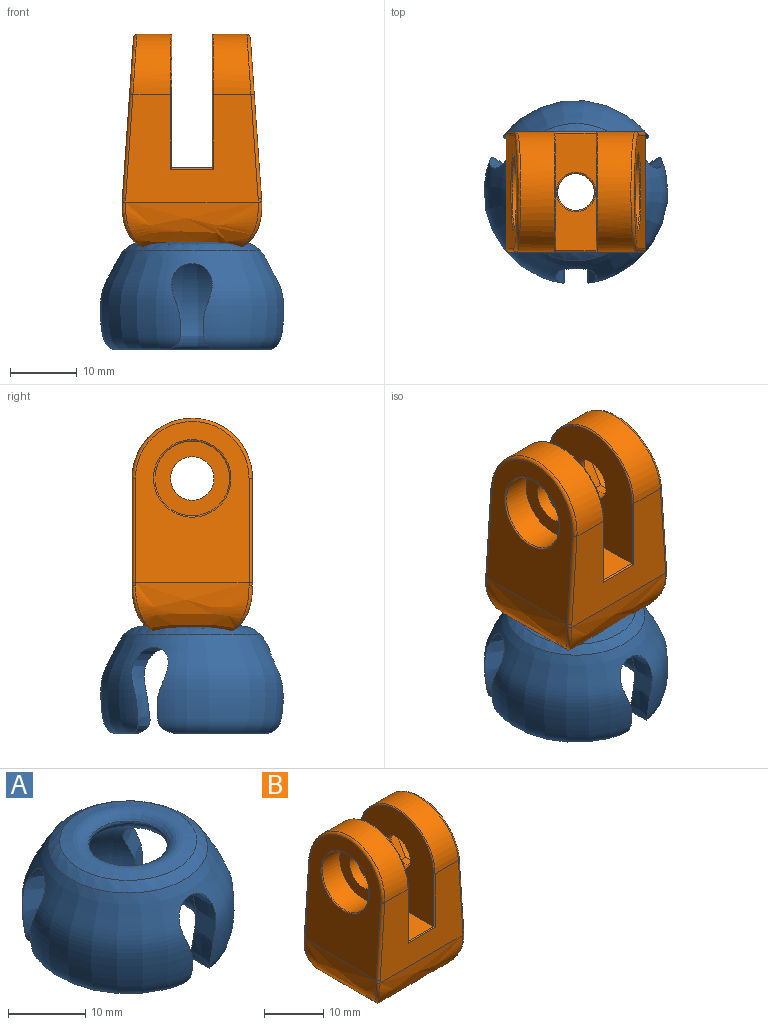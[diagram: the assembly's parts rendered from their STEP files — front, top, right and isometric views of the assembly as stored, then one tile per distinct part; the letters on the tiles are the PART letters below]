
ASSEMBLY  parts=2 mates=1
PART A: 9 faces, bbox 27.5x27.5x16.2 mm
  f0: revolved ~27.48x27.48mm, area 1956.7mm2, adj f1,f2,f3,f4,f5,f6,f7,f8
  f1: revolved ~20.56x20.56mm, area 105.4mm2, adj f0,f2
  f2: revolved ~17.76x17.76mm, area 177mm2, adj f0,f1
  f3: extruded ~12.89x6.51mm, area 55.8mm2, adj f0,f4
  f4: extruded ~12.89x6.51mm, area 55.8mm2, adj f0,f3
  f5: extruded ~12.89x7.44mm, area 55.8mm2, adj f0,f6
  f6: extruded ~12.89x7.44mm, area 55.8mm2, adj f0,f5
  f7: extruded ~12.89x7.44mm, area 55.8mm2, adj f0,f8
  f8: extruded ~12.89x7.44mm, area 55.8mm2, adj f0,f7
PART B: 57 faces, bbox 22x19.5x33.7 mm
  f0: plane 4.89x3mm, normal (0,-0.87,0.5), area 17mm2, adj f1,f5,f19,f21
  f1: plane 4.89x3mm, normal (0,-0.87,-0.5), area 17mm2, adj f0,f2,f19,f22
  f2: plane 5.65x3mm, normal (0,0,-1), area 16.9mm2, adj f1,f3,f19,f23
  f3: plane 4.89x3mm, normal (0,0.87,-0.5), area 17mm2, adj f2,f4,f19,f24
  f4: plane 4.89x3mm, normal (0,0.87,0.5), area 17mm2, adj f3,f5,f19,f25
  f5: plane 5.65x3mm, normal (0,0,1), area 16.9mm2, adj f0,f4,f19,f26
  f6: cylinder r=3.25mm len=6.5mm, axis (1,0,0), area 40.3mm2, adj f12,f19
  f7: cylinder r=9mm len=18mm, axis (-1,0,0), area 158.4mm2, adj f8,f11,f28,f38
  f8: plane 19.89x16.1mm, normal (0,-1,0), area 230.2mm2, adj f7,f10,f29,f32,f33,f34,f36,f45
  f9: cylinder r=3.25mm len=6.5mm, axis (1,0,0), area 40.3mm2, adj f13,f17
  f10: cylinder r=9mm len=18mm, axis (-1,0,0), area 158.4mm2, adj f8,f11,f31,f35
  f11: plane 19.89x16.1mm, normal (0,1,0), area 230.2mm2, adj f7,f10,f27,f30,f37,f39,f40,f46
  f12: plane 19.8x17.6mm, normal (-1,0,0), area 282.1mm2, adj f6,f14,f33,f35,f37
  f13: plane 19.8x17.6mm, normal (1,0,0), area 282.1mm2, adj f9,f14,f36,f38,f40
  f14: plane 17.6x6.05mm, normal (0,0,1), area 79.1mm2, adj f12,f13,f34,f39,f44
  f15: plane 24.09x17mm, normal (1,0,0.07), area 271.6mm2, adj f30,f31,f32,f41,f56
  f16: plane 24.09x17mm, normal (-1,0,0.07), area 273.4mm2, adj f27,f28,f29,f42,f47
  f17: plane 11.2x11.2mm, normal (-1,0,0), area 65.3mm2, adj f9,f18
  f18: cylinder r=5.6mm len=11.2mm, axis (1,0,0), area 145.2mm2, adj f17,f42
  f19: plane 11.3x9.79mm, normal (1,0,0), area 49.8mm2, adj f0,f1,f2,f3,f4,f5,f6
  f20: cylinder r=5.65mm len=11.3mm, axis (-1,0,0), area 40mm2, adj f21,f22,f23,f24,f25,f26,f41
  f21: plane 4.89x2.83mm, normal (1,0,0), area 2.9mm2, adj f0,f20
  f22: plane 4.89x2.83mm, normal (1,0,0), area 2.9mm2, adj f1,f20
  f23: plane 5.65x0.76mm, normal (1,0,0), area 2.9mm2, adj f2,f20
  f24: plane 4.89x2.83mm, normal (1,0,0), area 2.9mm2, adj f3,f20
  f25: plane 4.89x2.83mm, normal (1,0,0), area 2.9mm2, adj f4,f20
  f26: plane 5.65x0.76mm, normal (1,0,0), area 2.9mm2, adj f5,f20
  f27: cylinder r=0.5mm len=15.62mm, axis (0.07,0,1), area 12.3mm2, adj f11,f16,f28,f46
  f28: bspline ~18x10.56mm, area 21.2mm2, adj f7,f16,f27,f29
  f29: cylinder r=0.5mm len=15.62mm, axis (-0.07,0,-1), area 12.3mm2, adj f8,f16,f28,f45
  f30: cylinder r=0.5mm len=15.62mm, axis (0.07,0,-1), area 12.3mm2, adj f11,f15,f31,f54
  f31: bspline ~18x9mm, area 21.2mm2, adj f10,f15,f30,f32
  f32: cylinder r=0.5mm len=15.62mm, axis (-0.07,0,1), area 12.3mm2, adj f8,f15,f31,f53
  f33: cylinder r=0.2mm len=11.2mm, axis (0,0,-1), area 3.5mm2, adj f8,f12,f34,f35
  f34: cylinder r=0.2mm len=6.45mm, axis (-1,0,0), area 2mm2, adj f8,f14,f33,f36
  f35: torus R=8.8mm, axis (1,0,0), area 8.8mm2, adj f10,f12,f33,f37
  f36: cylinder r=0.2mm len=11.2mm, axis (0,0,1), area 3.5mm2, adj f8,f13,f34,f38
  f37: cylinder r=0.2mm len=11.2mm, axis (0,0,-1), area 3.5mm2, adj f11,f12,f35,f39
  f38: torus R=8.8mm, axis (1,0,0), area 8.8mm2, adj f7,f13,f36,f40
  f39: cylinder r=0.2mm len=6.45mm, axis (1,0,0), area 2mm2, adj f11,f14,f37,f40
  f40: cylinder r=0.2mm len=11.2mm, axis (0,0,1), area 3.5mm2, adj f11,f13,f38,f39
  f41: bspline ~11.7x11.7mm, area 11.3mm2, adj f15,f20
  f42: bspline ~11.6x11.6mm, area 11.2mm2, adj f16,f18
  f43: cylinder r=2.75mm len=12.8mm, axis (0,0,1), area 221.2mm2, adj f44,f47,f50,f51,f56
  f44: torus R=2.95mm, axis (0,0,1), area 5.6mm2, adj f14,f43
  f45: bspline ~2.63x0.61mm, area 0.4mm2, adj f8,f29,f47,f48
  f46: bspline ~2.63x0.61mm, area 0.4mm2, adj f11,f27,f47,f49
  f47: bspline ~17x8.47mm, area 163.6mm2, adj f16,f43,f45,f46,f48,f49
  f48: bspline ~8.75x7.93mm, area 6.7mm2, adj f45,f47,f50
  f49: bspline ~8.75x7.93mm, area 4.6mm2, adj f46,f47,f51
  f50: bspline ~20.1x7.9mm, area 159.7mm2, adj f8,f43,f48,f52
  f51: bspline ~20.1x7.9mm, area 159.7mm2, adj f11,f43,f49,f55
  f52: bspline ~8.34x7.93mm, area 6.7mm2, adj f50,f53,f56
  f53: bspline ~2.63x0.61mm, area 0.4mm2, adj f8,f32,f52,f56
  f54: bspline ~2.63x0.61mm, area 0.4mm2, adj f11,f30,f55,f56
  f55: bspline ~8.75x7.93mm, area 4.6mm2, adj f51,f54,f56
  f56: bspline ~17x8.47mm, area 162.7mm2, adj f15,f43,f52,f53,f54,f55
PLACE A t=(2.1,-0.09,6.38)mm fixed
PLACE B t=(2.1,-0.09,28.92)mm
MATE slider B.f43 <-> A.f0  axis (0,0,1) through (2.1,-0.09,4.92)mm
